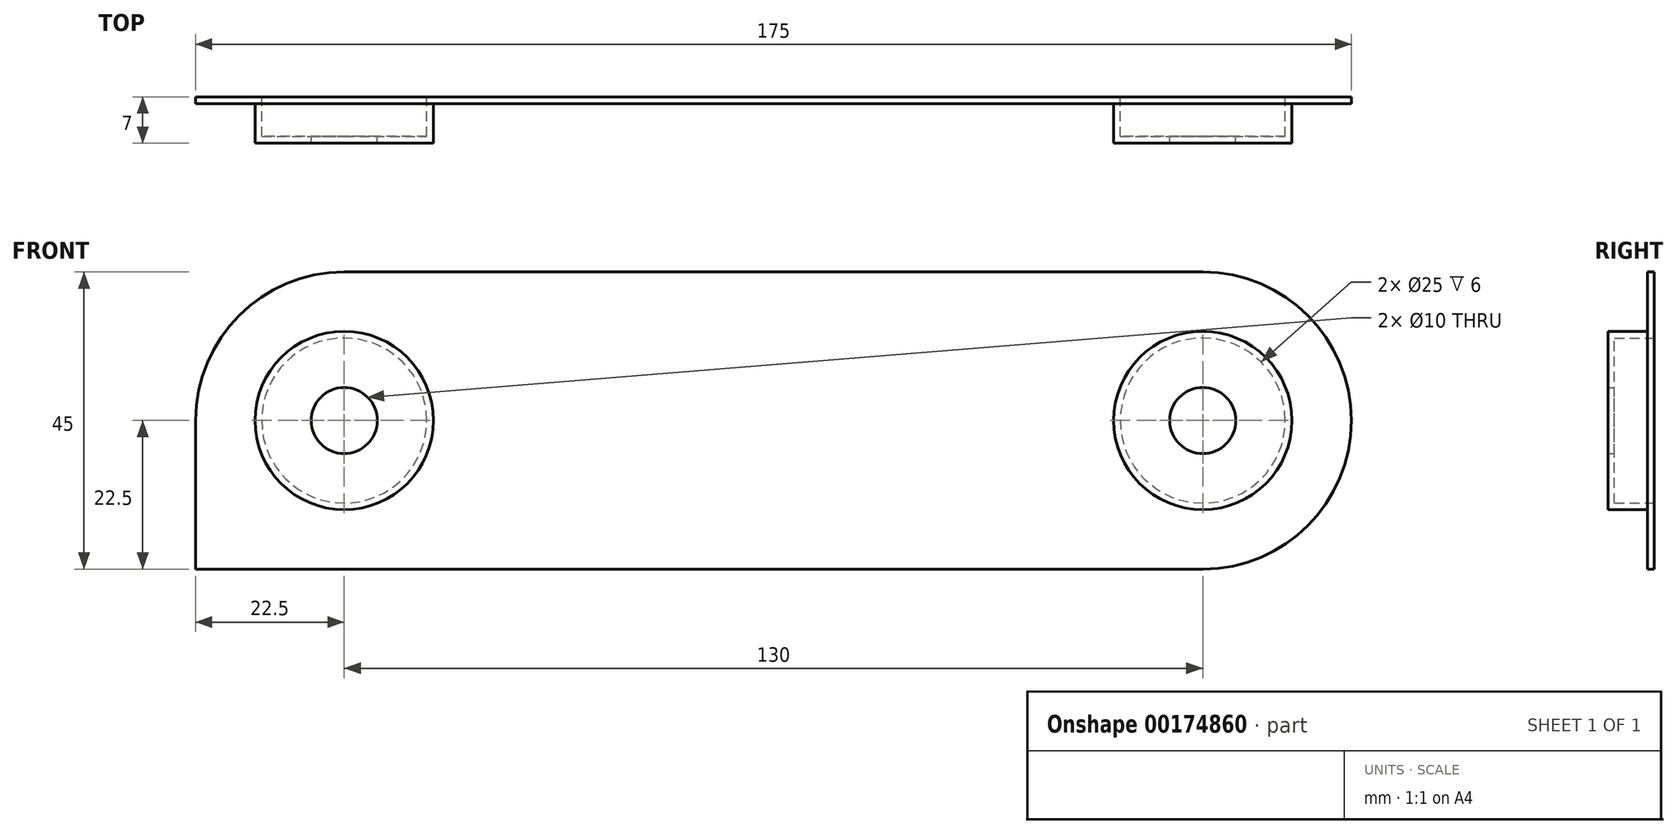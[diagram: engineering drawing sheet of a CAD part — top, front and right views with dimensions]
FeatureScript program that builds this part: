
annotation { "Feature Type Name" : "Feature", "Feature Type Description" : "" }
export const myFeature = defineFeature(function(context is Context, id is Id, definition is map)
    precondition{}
    {
        {
            var Q0;
            Q0=qCreatedBy(makeId("Front.planeOp"),FACE);
            var sketch = newSketch(context, id + "F0", { "sketchPlane" : qUnion([Q0])});
            skLineSegment(sketch, "E0.bottom", {"start": v(82.5, 22.5) * mm, "end": v(-82.5, 22.5) * mm});
            skLineSegment(sketch, "E0.top", {"start": v(82.5, -22.5) * mm, "end": v(-82.5, -22.5) * mm});
            skLineSegment(sketch, "E0.left", {"start": v(82.5, 22.5) * mm, "end": v(82.5, -22.5) * mm});
            skLineSegment(sketch, "E0.right", {"start": v(-82.5, 22.5) * mm, "end": v(-82.5, -22.5) * mm});
            skPoint(sketch, "E0.middle", {"position": v(0, 0) * mm});
            skCircle(sketch, "E1", {"center": v(-65, 0) * mm, "radius": 12.5 * mm});
            skCircle(sketch, "E2", {"center": v(65, 0) * mm, "radius": 12.5 * mm});
            skSolve(sketch);
        }
        {
            var Q0;
            Q0 = qSketchRegion(id + "F0", true);
            extrude(context, id + "F1", {"entities" : qUnion([Q0]), "depth" : 1 * mm});
        }
        {
            var Q0;
            Q0=makeQuery(id+"F1.opExtrude","CAP_FACE",FACE,{"disambiguationData":[OSD([sQuery(id+"F0.wireOp",EDGE,"E0.bottom"),sQuery(id+"F0.wireOp",EDGE,"E0.top"),sQuery(id+"F0.wireOp",EDGE,"E0.left"),sQuery(id+"F0.wireOp",EDGE,"E0.right"),sQuery(id+"F0.wireOp",EDGE,"E1"),sQuery(id+"F0.wireOp",EDGE,"E2")])],"isStart":false});
            var sketch = newSketch(context, id + "F2", { "sketchPlane" : qUnion([Q0])});
            skArc(sketch, "E3", {"start": v(65, -22.5) * mm, "mid": v(87.5, 0) * mm, "end": v(65, 22.5) * mm});
            skPoint(sketch, "E4.end.orphan", {"position": v(-82.5, 0) * mm});
            skArc(sketch, "E5", {"start": v(-65, 22.5) * mm, "mid": v(-87.5, 0) * mm, "end": v(-65, -22.5) * mm});
            skLineSegment(sketch, "E6", {"start": v(-65, 22.5) * mm, "end": v(-65, 14.96) * mm});
            skLineSegment(sketch, "E7", {"start": v(-65, 14.96) * mm, "end": v(-75.45, 11.76) * mm});
            skLineSegment(sketch, "E8", {"start": v(-75.45, 11.76) * mm, "end": v(-79.56, 6.47) * mm});
            skLineSegment(sketch, "E9", {"start": v(-79.56, 6.47) * mm, "end": v(-79.56, 0) * mm});
            skLineSegment(sketch, "E10", {"start": v(-79.56, 0) * mm, "end": v(-76.59, -7.8) * mm});
            skLineSegment(sketch, "E11", {"start": v(-76.59, -7.8) * mm, "end": v(-72.84, -12.91) * mm});
            skLineSegment(sketch, "E12", {"start": v(-72.84, -12.91) * mm, "end": v(-67.48, -15.7) * mm});
            skLineSegment(sketch, "E13", {"start": v(-67.48, -15.7) * mm, "end": v(-65, -22.5) * mm});
            skLineSegment(sketch, "E14", {"start": v(65, 22.5) * mm, "end": v(71.47, 16.28) * mm});
            skLineSegment(sketch, "E15", {"start": v(71.47, 16.28) * mm, "end": v(77.4, 9.11) * mm});
            skLineSegment(sketch, "E16", {"start": v(77.4, 9.11) * mm, "end": v(80.4, 2.14) * mm});
            skLineSegment(sketch, "E17", {"start": v(80.4, 2.14) * mm, "end": v(80.4, -5.23) * mm});
            skLineSegment(sketch, "E18", {"start": v(80.4, -5.23) * mm, "end": v(78.4, -12.15) * mm});
            skLineSegment(sketch, "E19", {"start": v(78.4, -12.15) * mm, "end": v(74.66, -14.4) * mm});
            skLineSegment(sketch, "E20", {"start": v(74.66, -14.4) * mm, "end": v(68.4, -19.1) * mm});
            skLineSegment(sketch, "E21", {"start": v(68.4, -19.1) * mm, "end": v(65, -22.5) * mm});
            skSolve(sketch);
        }
        {
            var Q0;
            Q0 = qSketchRegion(id + "F2", true);
            extrude(context, id + "F3", {"entities" : qUnion([Q0]), "operationType" : NewBodyOperationType.ADD, "oppositeDirection" : true, "depth" : 1 * mm});
        }
        {
            var Q0;
            {var subQ1=makeQuery(id+"F1.opExtrude","CAP_EDGE",EDGE,{"disambiguationData":[OSD([sQuery(id+"F0.wireOp",EDGE,"E0.bottom")])],"isStart":false});var subQ3=makeQuery(id+"F1.opExtrude","CAP_EDGE",EDGE,{"disambiguationData":[OSD([sQuery(id+"F0.wireOp",EDGE,"E0.right")])],"isStart":false});var subQ5=makeQuery(id+"F2.imprint","INTERSECT",VERTEX,{"derivedFrom":[subQ1,subQ3]});Q0=makeQuery(id+"F2.imprint","IMPRINT",FACE,{"disambiguationData":[TD([[makeQuery(id+"F2.imprint","IMPRINT",EDGE,{"disambiguationData":[TD([[subQ5,-1.0]])],"derivedFrom":subQ3}),1.0]])]});}
            extrude(context, id + "F4", {"entities" : qUnion([Q0]), "operationType" : NewBodyOperationType.REMOVE, "oppositeDirection" : true, "depth" : 25 * mm});
        }
        {
            var Q0;
            {var subQ1=makeQuery(id+"F1.opExtrude","CAP_EDGE",EDGE,{"disambiguationData":[OSD([sQuery(id+"F0.wireOp",EDGE,"E0.top")])],"isStart":false});var subQ3=makeQuery(id+"F1.opExtrude","CAP_EDGE",EDGE,{"disambiguationData":[OSD([sQuery(id+"F0.wireOp",EDGE,"E0.left")])],"isStart":false});var subQ5=makeQuery(id+"F2.imprint","INTERSECT",VERTEX,{"derivedFrom":[subQ1,subQ3]});Q0=makeQuery(id+"F2.imprint","IMPRINT",FACE,{"disambiguationData":[TD([[makeQuery(id+"F2.imprint","IMPRINT",EDGE,{"disambiguationData":[TD([[subQ5,1.0]])],"derivedFrom":subQ3}),-1.0]])]});}
            var Q1;
            {var subQ1=makeQuery(id+"F1.opExtrude","CAP_EDGE",EDGE,{"disambiguationData":[OSD([sQuery(id+"F0.wireOp",EDGE,"E0.bottom")])],"isStart":false});var subQ3=makeQuery(id+"F1.opExtrude","CAP_EDGE",EDGE,{"disambiguationData":[OSD([sQuery(id+"F0.wireOp",EDGE,"E0.left")])],"isStart":false});var subQ5=makeQuery(id+"F2.imprint","INTERSECT",VERTEX,{"derivedFrom":[subQ1,subQ3]});Q1=makeQuery(id+"F2.imprint","IMPRINT",FACE,{"disambiguationData":[TD([[makeQuery(id+"F2.imprint","IMPRINT",EDGE,{"disambiguationData":[TD([[subQ5,-1.0]])],"derivedFrom":subQ3}),-1.0]])]});}
            var Q2;
            {var subQ1=makeQuery(id+"F1.opExtrude","CAP_EDGE",EDGE,{"disambiguationData":[OSD([sQuery(id+"F0.wireOp",EDGE,"E0.top")])],"isStart":false});var subQ3=makeQuery(id+"F1.opExtrude","CAP_EDGE",EDGE,{"disambiguationData":[OSD([sQuery(id+"F0.wireOp",EDGE,"E0.right")])],"isStart":false});var subQ5=makeQuery(id+"F2.imprint","INTERSECT",VERTEX,{"derivedFrom":[subQ1,subQ3]});Q2=makeQuery(id+"F2.imprint","IMPRINT",FACE,{"disambiguationData":[TD([[makeQuery(id+"F2.imprint","IMPRINT",EDGE,{"disambiguationData":[TD([[subQ5,1.0]])],"derivedFrom":subQ3}),1.0]])]});}
            extrude(context, id + "F5", {"entities" : qUnion([Q0, Q1, Q2]), "operationType" : NewBodyOperationType.REMOVE, "oppositeDirection" : true, "depth" : 25 * mm});
        }
        {
            var Q0;
            Q0=makeQuery(id+"F3.boolean.opBoolean","MERGE",FACE,{"derivedFrom":[makeQuery(id+"F1.opExtrude","CAP_FACE",FACE,{"disambiguationData":[OSD([sQuery(id+"F0.wireOp",EDGE,"E0.bottom"),sQuery(id+"F0.wireOp",EDGE,"E0.top"),sQuery(id+"F0.wireOp",EDGE,"E0.left"),sQuery(id+"F0.wireOp",EDGE,"E0.right"),sQuery(id+"F0.wireOp",EDGE,"E1"),sQuery(id+"F0.wireOp",EDGE,"E2")])],"isStart":false}),makeQuery(id+"F3.opExtrude","CAP_FACE",FACE,{"disambiguationData":[OSD([sQuery(id+"F2.wireOp",EDGE,"E3"),sQuery(id+"F2.wireOp",EDGE,"E14"),sQuery(id+"F2.wireOp",EDGE,"E15"),sQuery(id+"F2.wireOp",EDGE,"E16"),sQuery(id+"F2.wireOp",EDGE,"E17"),sQuery(id+"F2.wireOp",EDGE,"E18"),sQuery(id+"F2.wireOp",EDGE,"E19"),sQuery(id+"F2.wireOp",EDGE,"E20"),sQuery(id+"F2.wireOp",EDGE,"E21")])],"isStart":true}),makeQuery(id+"F3.opExtrude","CAP_FACE",FACE,{"disambiguationData":[OSD([sQuery(id+"F2.wireOp",EDGE,"E5"),sQuery(id+"F2.wireOp",EDGE,"E6"),sQuery(id+"F2.wireOp",EDGE,"E7"),sQuery(id+"F2.wireOp",EDGE,"E8"),sQuery(id+"F2.wireOp",EDGE,"E9"),sQuery(id+"F2.wireOp",EDGE,"E10"),sQuery(id+"F2.wireOp",EDGE,"E11"),sQuery(id+"F2.wireOp",EDGE,"E12"),sQuery(id+"F2.wireOp",EDGE,"E13")])],"isStart":true})]});
            var sketch = newSketch(context, id + "F6", { "sketchPlane" : qUnion([Q0])});
            skCircle(sketch, "E22", {"center": v(-65, 0) * mm, "radius": 12.5 * mm});
            skCircle(sketch, "E23", {"center": v(-65, 0) * mm, "radius": 13.5 * mm});
            skCircle(sketch, "E24", {"center": v(65, 0) * mm, "radius": 12.5 * mm});
            skCircle(sketch, "E25", {"center": v(65, 0) * mm, "radius": 13.5 * mm});
            skSolve(sketch);
        }
        {
            var Q0;
            Q0 = qSketchRegion(id + "F6", true);
            extrude(context, id + "F7", {"entities" : qUnion([Q0]), "operationType" : NewBodyOperationType.ADD, "depth" : 5 * mm});
        }
        {
            var Q0;
            Q0=makeQuery(id+"F7.opExtrude","CAP_FACE",FACE,{"disambiguationData":[OSD([sQuery(id+"F6.wireOp",EDGE,"E22"),sQuery(id+"F6.wireOp",EDGE,"E23")])],"isStart":false});
            var sketch = newSketch(context, id + "F8", { "sketchPlane" : qUnion([Q0])});
            skCircle(sketch, "E26", {"center": v(-65, 0) * mm, "radius": 13.5 * mm});
            skCircle(sketch, "E27", {"center": v(-65, 0) * mm, "radius": 5 * mm});
            skCircle(sketch, "E28", {"center": v(65, 0) * mm, "radius": 13.5 * mm});
            skCircle(sketch, "E29", {"center": v(65, 0) * mm, "radius": 5 * mm});
            skSolve(sketch);
        }
        {
            var Q0;
            Q0 = qSketchRegion(id + "F8", true);
            extrude(context, id + "F9", {"entities" : qUnion([Q0]), "operationType" : NewBodyOperationType.ADD, "depth" : 1 * mm});
        }
        {
            var Q0;
            Q0=makeQuery(id+"F3.boolean.opBoolean","MERGE",FACE,{"derivedFrom":[makeQuery(id+"F1.opExtrude","CAP_FACE",FACE,{"disambiguationData":[OSD([sQuery(id+"F0.wireOp",EDGE,"E0.bottom"),sQuery(id+"F0.wireOp",EDGE,"E0.top"),sQuery(id+"F0.wireOp",EDGE,"E0.left"),sQuery(id+"F0.wireOp",EDGE,"E0.right"),sQuery(id+"F0.wireOp",EDGE,"E1"),sQuery(id+"F0.wireOp",EDGE,"E2")])],"isStart":false}),makeQuery(id+"F3.opExtrude","CAP_FACE",FACE,{"disambiguationData":[OSD([sQuery(id+"F2.wireOp",EDGE,"E3"),sQuery(id+"F2.wireOp",EDGE,"E14"),sQuery(id+"F2.wireOp",EDGE,"E15"),sQuery(id+"F2.wireOp",EDGE,"E16"),sQuery(id+"F2.wireOp",EDGE,"E17"),sQuery(id+"F2.wireOp",EDGE,"E18"),sQuery(id+"F2.wireOp",EDGE,"E19"),sQuery(id+"F2.wireOp",EDGE,"E20"),sQuery(id+"F2.wireOp",EDGE,"E21")])],"isStart":true}),makeQuery(id+"F3.opExtrude","CAP_FACE",FACE,{"disambiguationData":[OSD([sQuery(id+"F2.wireOp",EDGE,"E5"),sQuery(id+"F2.wireOp",EDGE,"E6"),sQuery(id+"F2.wireOp",EDGE,"E7"),sQuery(id+"F2.wireOp",EDGE,"E8"),sQuery(id+"F2.wireOp",EDGE,"E9"),sQuery(id+"F2.wireOp",EDGE,"E10"),sQuery(id+"F2.wireOp",EDGE,"E11"),sQuery(id+"F2.wireOp",EDGE,"E12"),sQuery(id+"F2.wireOp",EDGE,"E13")])],"isStart":true})]});
            var sketch = newSketch(context, id + "F10", { "sketchPlane" : qUnion([Q0])});
            skLineSegment(sketch, "E30.bottom", {"start": v(-87.5, 0) * mm, "end": v(-81.94, 0) * mm});
            skLineSegment(sketch, "E30.top", {"start": v(-87.5, -22.5) * mm, "end": v(-65, -22.5) * mm});
            skLineSegment(sketch, "E30.left", {"start": v(-87.5, 0) * mm, "end": v(-87.5, -22.5) * mm});
            skLineSegment(sketch, "E30.right", {"start": v(-65, -18.59) * mm, "end": v(-65, -22.5) * mm});
            skLineSegment(sketch, "E31", {"start": v(-81.94, 0) * mm, "end": v(-80.2, -9.62) * mm});
            skLineSegment(sketch, "E32", {"start": v(-80.2, -9.62) * mm, "end": v(-73.32, -16) * mm});
            skLineSegment(sketch, "E33", {"start": v(-73.32, -16) * mm, "end": v(-65, -18.59) * mm});
            skSolve(sketch);
        }
        {
            var Q0;
            Q0 = qSketchRegion(id + "F10", true);
            extrude(context, id + "F11", {"entities" : qUnion([Q0]), "operationType" : NewBodyOperationType.ADD, "oppositeDirection" : true, "depth" : 1 * mm});
        }
    });
